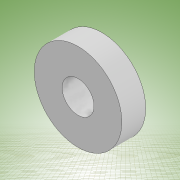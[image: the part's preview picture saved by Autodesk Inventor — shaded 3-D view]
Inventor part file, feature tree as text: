
AUTODESK INVENTOR PART (.ipt)
format: ipt  version: 2022 (Build 260153000, 153)  size: 110,080 bytes
history: native  units: mm
features: other x1, extrude x1, sketch x1
ambient origin geometry x8: Origin, YZ Plane, XZ Plane, XY Plane, X Axis, Y Axis, Z Axis, Center Point
bodies: Body1 (feature_tree)
feature tree (3):
  other  "Sólido1"
  extrude  "Extrusión1"  Depth=6.0mm
  sketch  "Boceto1"  dims[d0=22.0mm d1=8.0mm d2=6.0mm d3=0.0mm]
